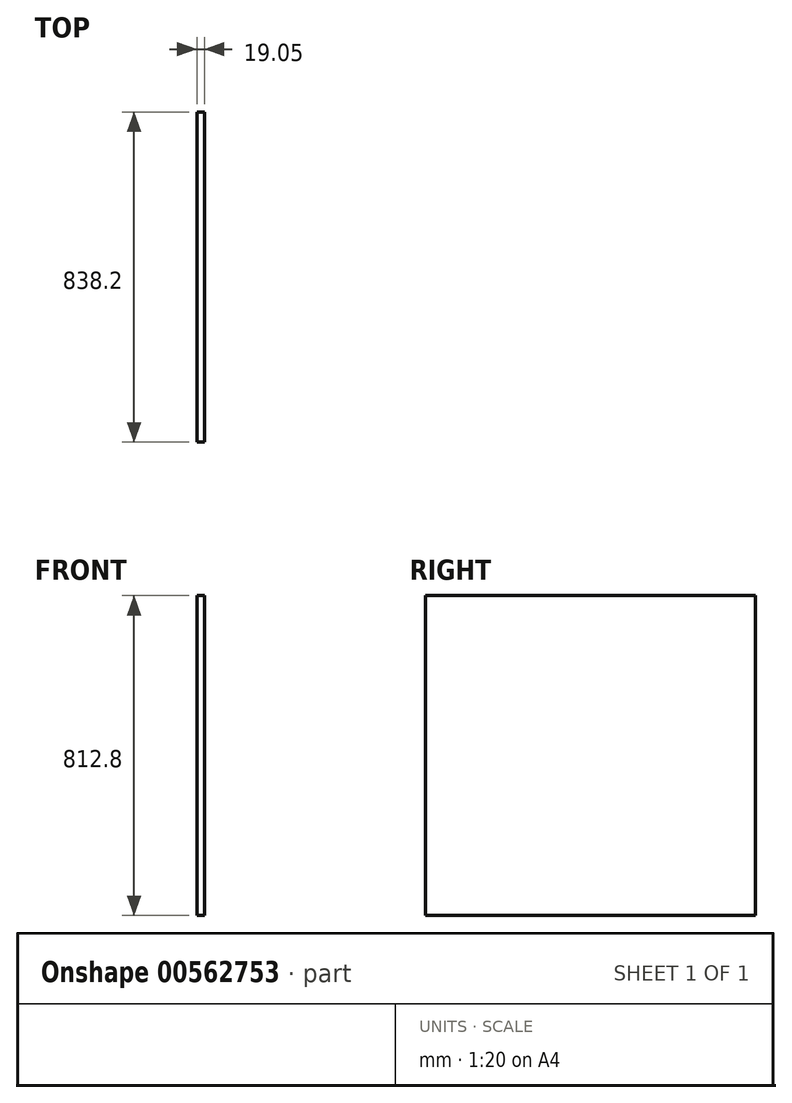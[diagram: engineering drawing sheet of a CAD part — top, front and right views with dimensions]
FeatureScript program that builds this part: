
annotation { "Feature Type Name" : "Feature", "Feature Type Description" : "" }
export const myFeature = defineFeature(function(context is Context, id is Id, definition is map)
    precondition{}
    {
        {
            var Q0;
            Q0=qCreatedBy(makeId("Right.planeOp"),FACE);
            var sketch = newSketch(context, id + "F0", { "sketchPlane" : qUnion([Q0])});
            skLineSegment(sketch, "E0.bottom", {"start": v(-419.1, -406.4) * mm, "end": v(419.1, -406.4) * mm});
            skLineSegment(sketch, "E0.top", {"start": v(-419.1, 406.4) * mm, "end": v(419.1, 406.4) * mm});
            skLineSegment(sketch, "E0.left", {"start": v(-419.1, -406.4) * mm, "end": v(-419.1, 406.4) * mm});
            skLineSegment(sketch, "E0.right", {"start": v(419.1, -406.4) * mm, "end": v(419.1, 406.4) * mm});
            skPoint(sketch, "E0.middle", {"position": v(0, 0) * mm});
            skSolve(sketch);
        }
        {
            var Q0;
            Q0 = qSketchRegion(id + "F0", true);
            extrude(context, id + "F1", {"entities" : qUnion([Q0]), "depth" : 19.05 * mm, "offsetDistance" : 25.4 * mm});
        }
    });
